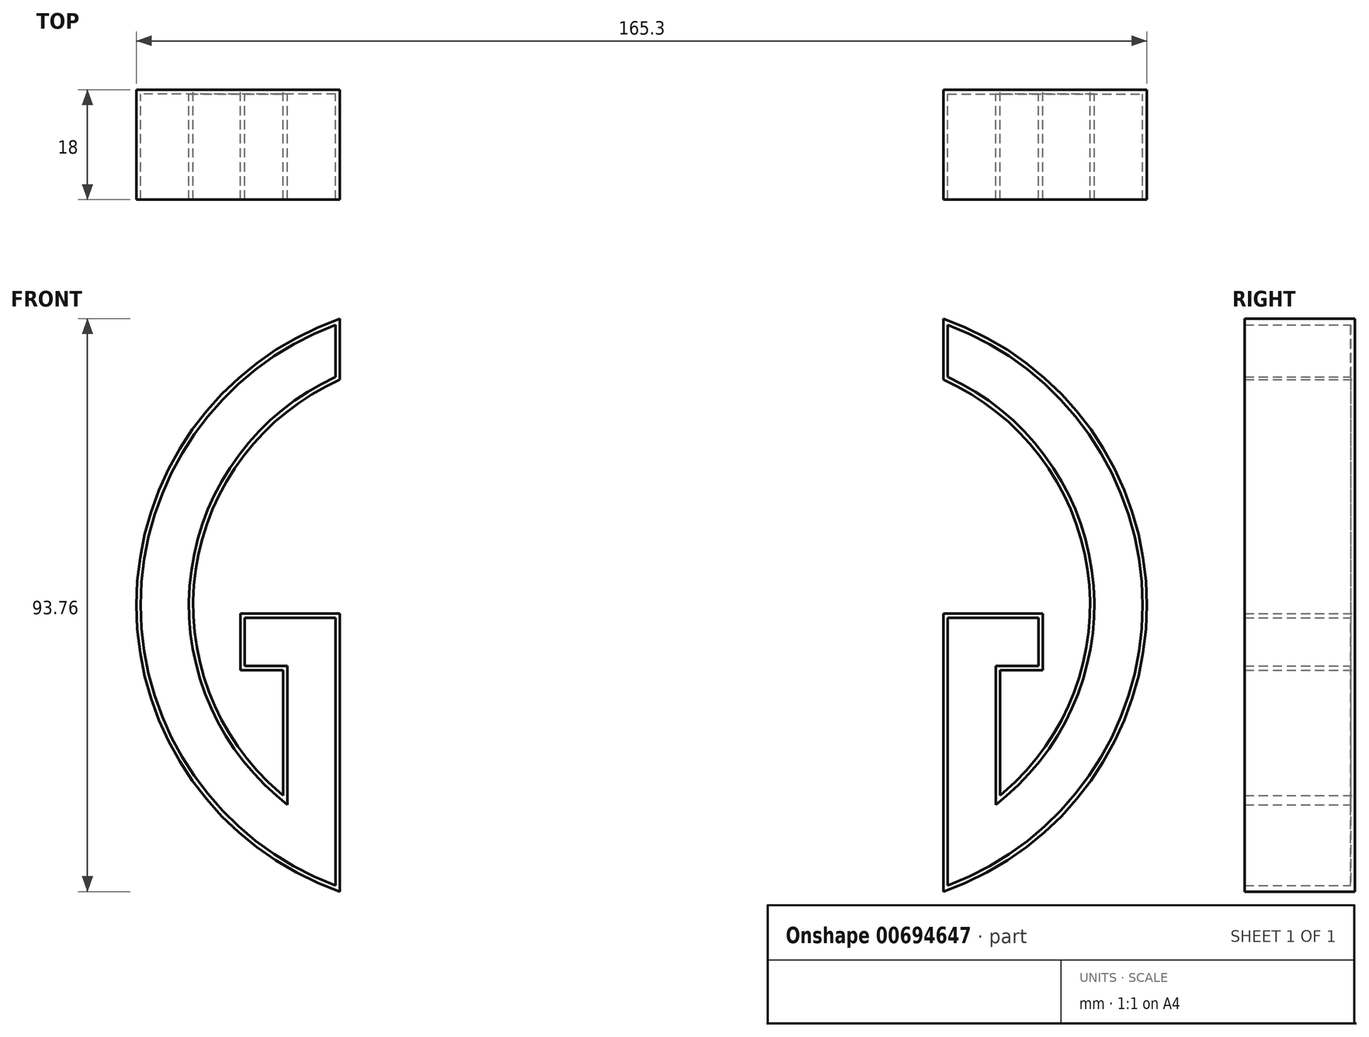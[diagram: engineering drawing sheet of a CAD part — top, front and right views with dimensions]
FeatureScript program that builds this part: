
annotation { "Feature Type Name" : "Feature", "Feature Type Description" : "" }
export const myFeature = defineFeature(function(context is Context, id is Id, definition is map)
    precondition{}
    {
        {
            var Q0;
            Q0=qCreatedBy(makeId("Front.planeOp"),FACE);
            var sketch = newSketch(context, id + "F0", { "sketchPlane" : qUnion([Q0])});
            skArc(sketch, "E0", {"start": v(-49.35, 46.87) * mm, "mid": v(-82.65, 0) * mm, "end": v(-49.35, -46.89) * mm});
            skLineSegment(sketch, "E1", {"start": v(-49.35, -46.89) * mm, "end": v(-49.35, -1.36) * mm});
            skLineSegment(sketch, "E2", {"start": v(-49.35, -1.36) * mm, "end": v(-65.65, -1.36) * mm});
            skLineSegment(sketch, "E3", {"start": v(-65.65, -1.36) * mm, "end": v(-65.65, -10.66) * mm});
            skLineSegment(sketch, "E4", {"start": v(-65.65, -10.66) * mm, "end": v(-58.65, -10.66) * mm});
            skLineSegment(sketch, "E5", {"start": v(-58.65, -10.66) * mm, "end": v(-58.65, -31.16) * mm});
            skLineSegment(sketch, "E6", {"start": v(-58.65, -31.16) * mm, "end": v(-59.23, -30.67) * mm});
            skArc(sketch, "E7", {"start": v(-49.35, 36.88) * mm, "mid": v(-72.93, 5.83) * mm, "end": v(-59.23, -30.67) * mm});
            skLineSegment(sketch, "E8", {"start": v(-49.35, 36.88) * mm, "end": v(-49.35, 46.87) * mm});
            skArc(sketch, "E9", {"start": v(-50.6, 45.08) * mm, "mid": v(-81.4, 0) * mm, "end": v(-50.6, -45.1) * mm});
            skLineSegment(sketch, "E10", {"start": v(-50.6, -45.1) * mm, "end": v(-50.6, -2.6) * mm});
            skLineSegment(sketch, "E11", {"start": v(-50.6, -2.6) * mm, "end": v(-64.4, -2.6) * mm});
            skLineSegment(sketch, "E12", {"start": v(-64.4, -2.6) * mm, "end": v(-64.4, -9.4) * mm});
            skLineSegment(sketch, "E13", {"start": v(-64.4, -9.4) * mm, "end": v(-57.4, -9.4) * mm});
            skLineSegment(sketch, "E14", {"start": v(-57.4, -9.4) * mm, "end": v(-57.4, -33.88) * mm});
            skLineSegment(sketch, "E15", {"start": v(-57.4, -33.88) * mm, "end": v(-60.04, -31.62) * mm});
            skArc(sketch, "E16", {"start": v(-50.6, 37.69) * mm, "mid": v(-74.22, 5.6) * mm, "end": v(-60.04, -31.62) * mm});
            skLineSegment(sketch, "E17", {"start": v(-50.6, 37.69) * mm, "end": v(-50.6, 45.08) * mm});
            skArc(sketch, "E18", {"start": v(-50.95, 44.56) * mm, "mid": v(-81.05, 0) * mm, "end": v(-50.95, -44.58) * mm});
            skLineSegment(sketch, "E19", {"start": v(-50.95, -44.58) * mm, "end": v(-50.95, -2.96) * mm});
            skLineSegment(sketch, "E20", {"start": v(-50.95, -2.96) * mm, "end": v(-64.05, -2.96) * mm});
            skLineSegment(sketch, "E21", {"start": v(-64.05, -2.96) * mm, "end": v(-64.05, -9.06) * mm});
            skLineSegment(sketch, "E22", {"start": v(-64.05, -9.06) * mm, "end": v(-57.05, -9.06) * mm});
            skLineSegment(sketch, "E23", {"start": v(-57.05, -9.06) * mm, "end": v(-57.05, -34.64) * mm});
            skLineSegment(sketch, "E24", {"start": v(-57.05, -34.64) * mm, "end": v(-60.27, -31.89) * mm});
            skArc(sketch, "E25", {"start": v(-50.95, 37.9) * mm, "mid": v(-74.58, 5.54) * mm, "end": v(-60.27, -31.89) * mm});
            skLineSegment(sketch, "E26", {"start": v(-50.95, 37.9) * mm, "end": v(-50.95, 44.56) * mm});
            skSolve(sketch);
        }
        {
            var Q0;
            Q0 = qSketchRegion(id + "F0", true);
            var Q1;
            Q1=makeQuery(id+"F0.imprint","IMPRINT",FACE,{"disambiguationData":[TD([[makeQuery(id+"F0.imprint","IMPRINT",EDGE,{"derivedFrom":sQuery(id+"F0.wireOp",EDGE,"E18")}),1.0]])]});
            var Q2;
            Q2=makeQuery(id+"F0.imprint","IMPRINT",FACE,{"disambiguationData":[TD([[makeQuery(id+"F0.imprint","IMPRINT",EDGE,{"derivedFrom":sQuery(id+"F0.wireOp",EDGE,"E9")}),1.0]])]});
            extrude(context, id + "F1", {"entities" : qUnion([Q0, Q1, Q2]), "depth" : 18 * mm, "offsetDistance" : 25 * mm});
        }
        {
            var Q0;
            Q0=makeQuery(id+"F1.opExtrude","CAP_FACE",FACE,{"disambiguationData":[OSD([sQuery(id+"F0.wireOp",EDGE,"E0"),sQuery(id+"F0.wireOp",EDGE,"E1"),sQuery(id+"F0.wireOp",EDGE,"E2"),sQuery(id+"F0.wireOp",EDGE,"E3"),sQuery(id+"F0.wireOp",EDGE,"E4"),sQuery(id+"F0.wireOp",EDGE,"E5"),sQuery(id+"F0.wireOp",EDGE,"E6"),sQuery(id+"F0.wireOp",EDGE,"E7"),sQuery(id+"F0.wireOp",EDGE,"E8")])],"isStart":false});
            shell(context, id + "F2", {"entities" : qUnion([Q0]), "thickness" : 0.7 * mm});
        }
        {
            var Q0;
            Q0=makeQuery(id+"F1.opExtrude","SWEPT_BODY",BODY,{"disambiguationData":[OSD([sQuery(id+"F0.wireOp",EDGE,"E0"),sQuery(id+"F0.wireOp",EDGE,"E1"),sQuery(id+"F0.wireOp",EDGE,"E2"),sQuery(id+"F0.wireOp",EDGE,"E3"),sQuery(id+"F0.wireOp",EDGE,"E4"),sQuery(id+"F0.wireOp",EDGE,"E5"),sQuery(id+"F0.wireOp",EDGE,"E6"),sQuery(id+"F0.wireOp",EDGE,"E7"),sQuery(id+"F0.wireOp",EDGE,"E8")])]});
            var Q1;
            Q1=qCreatedBy(makeId("Right.planeOp"),FACE);
            mirror(context, id + "F3", {"entities" : qUnion([Q0]), "mirrorPlane" : qUnion([Q1])});
        }
    });
